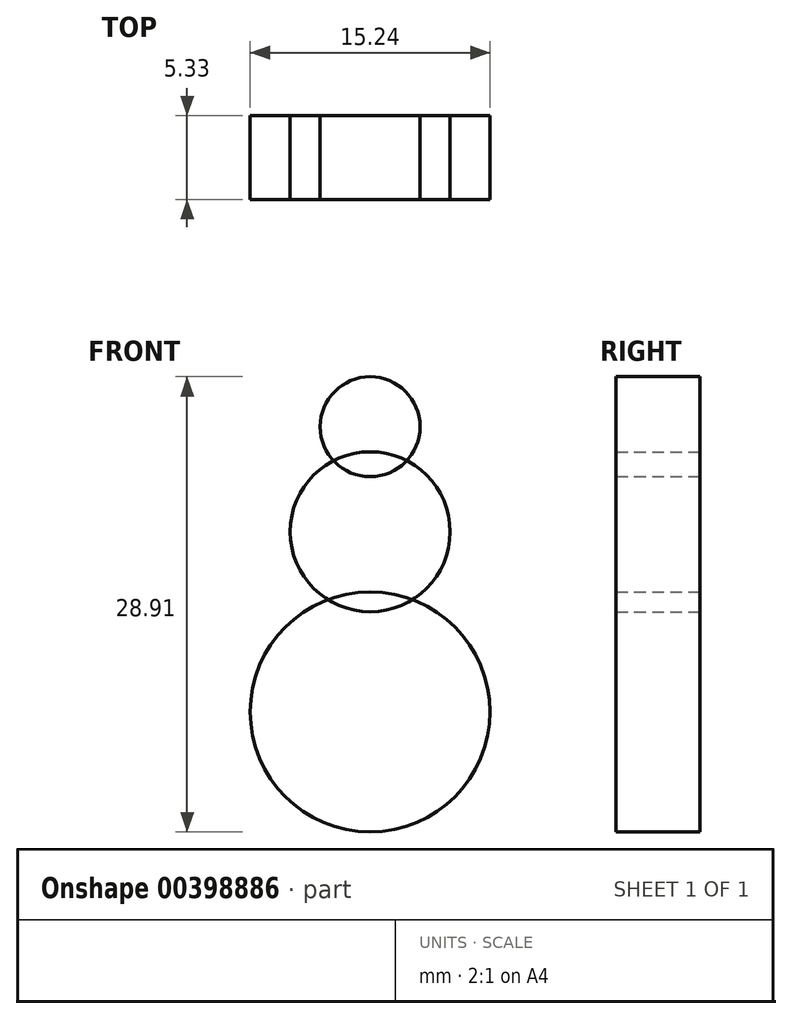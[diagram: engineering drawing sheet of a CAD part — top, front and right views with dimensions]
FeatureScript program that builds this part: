
annotation { "Feature Type Name" : "Feature", "Feature Type Description" : "" }
export const myFeature = defineFeature(function(context is Context, id is Id, definition is map)
    precondition{}
    {
        {
            var Q0;
            Q0=qCreatedBy(makeId("Front.planeOp"),FACE);
            var sketch = newSketch(context, id + "F0", { "sketchPlane" : qUnion([Q0])});
            skCircle(sketch, "E0", {"center": v(0, 0) * mm, "radius": 7.62 * mm});
            skSolve(sketch);
        }
        {
            var Q0;
            Q0=qCreatedBy(makeId("Front.planeOp"),FACE);
            var sketch = newSketch(context, id + "F1", { "sketchPlane" : qUnion([Q0])});
            skCircle(sketch, "E1", {"center": v(0, 11.44) * mm, "radius": 5.08 * mm});
            skSolve(sketch);
        }
        {
            var Q0;
            Q0=qCreatedBy(makeId("Front.planeOp"),FACE);
            var sketch = newSketch(context, id + "F2", { "sketchPlane" : qUnion([Q0])});
            skCircle(sketch, "E2", {"center": v(0, 18.11) * mm, "radius": 3.17 * mm});
            skSolve(sketch);
        }
        {
            var Q0;
            Q0=makeQuery(id+"F2.imprint","IMPRINT",FACE,{"disambiguationData":[TD([[makeQuery(id+"F2.imprint","IMPRINT",EDGE,{"derivedFrom":sQuery(id+"F2.wireOp",EDGE,"E2")}),1.0]])]});
            var Q1;
            Q1=makeQuery(id+"F1.imprint","IMPRINT",FACE,{"disambiguationData":[TD([[makeQuery(id+"F1.imprint","IMPRINT",EDGE,{"derivedFrom":sQuery(id+"F1.wireOp",EDGE,"E1")}),1.0]])]});
            var Q2;
            Q2=makeQuery(id+"F0.imprint","IMPRINT",FACE,{"disambiguationData":[TD([[makeQuery(id+"F0.imprint","IMPRINT",EDGE,{"derivedFrom":sQuery(id+"F0.wireOp",EDGE,"E0")}),1.0]])]});
            extrude(context, id + "F3", {"entities" : qUnion([Q0, Q1, Q2]), "depth" : 5.33 * mm});
        }
    });
